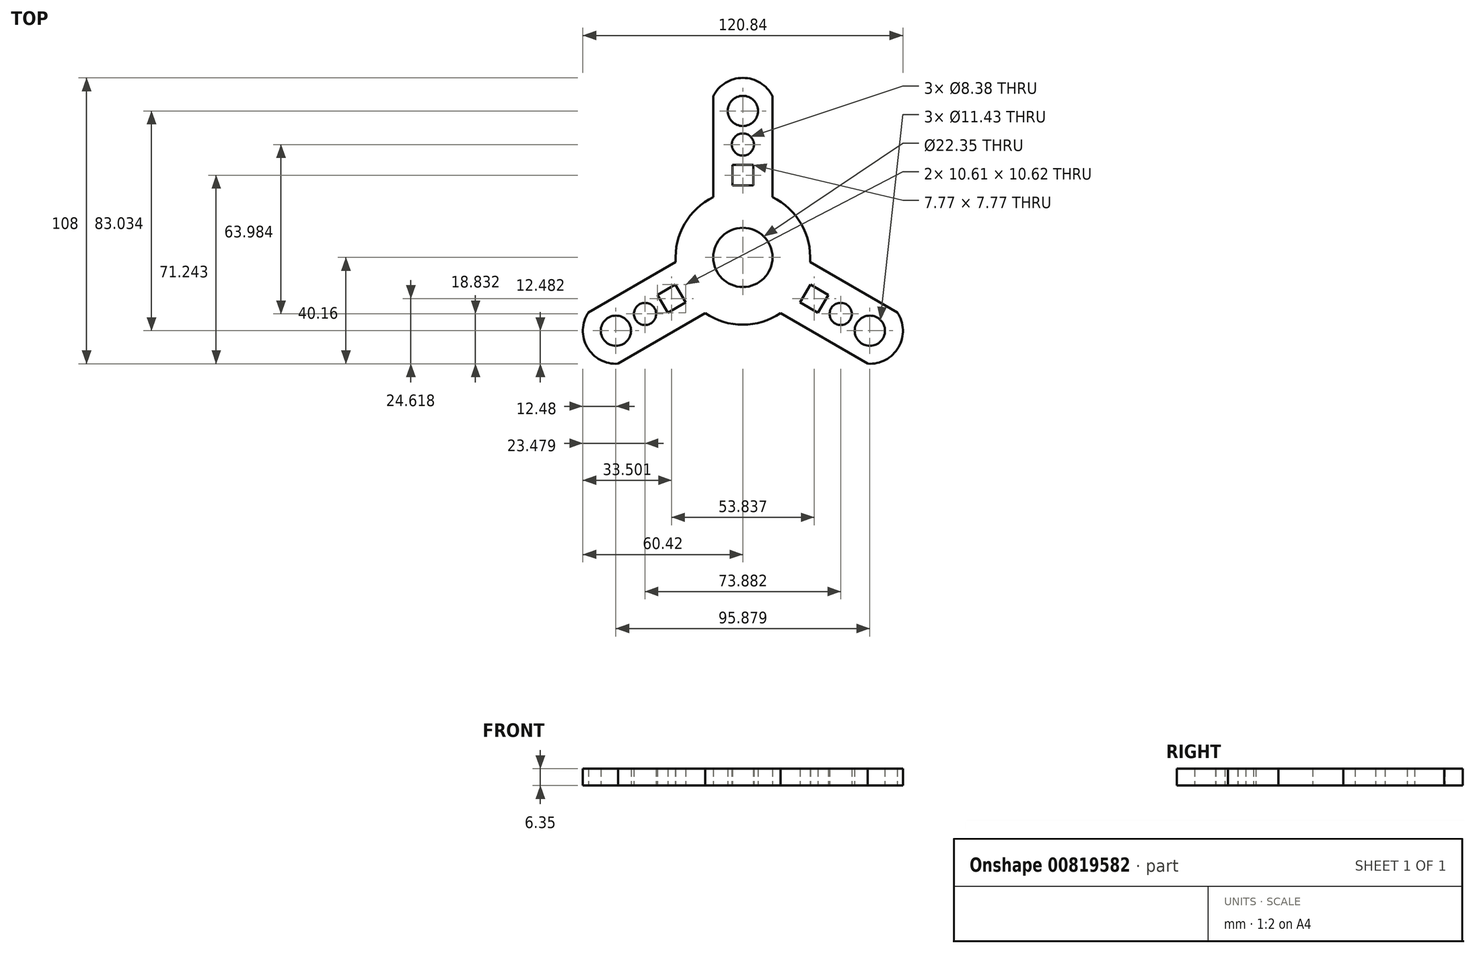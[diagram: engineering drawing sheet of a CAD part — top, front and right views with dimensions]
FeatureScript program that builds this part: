
annotation { "Feature Type Name" : "Feature", "Feature Type Description" : "" }
export const myFeature = defineFeature(function(context is Context, id is Id, definition is map)
    precondition{}
    {
        {
            var Q0;
            Q0=qCreatedBy(makeId("Top.planeOp"),FACE);
            var sketch = newSketch(context, id + "F0", { "sketchPlane" : qUnion([Q0])});
            skCircle(sketch, "E0", {"center": v(0, 0) * mm, "radius": 25.4 * mm});
            skCircle(sketch, "E1", {"center": v(0, 0) * mm, "radius": 11.18 * mm});
            skLineSegment(sketch, "E2", {"start": v(-11.18, 22.8) * mm, "end": v(-11.18, 60.9) * mm});
            skPoint(sketch, "E3.orphan", {"position": v(-11.18, 0) * mm});
            skLineSegment(sketch, "E4.MirrorCS", {"start": v(11.18, 22.8) * mm, "end": v(11.18, 60.9) * mm});
            skArc(sketch, "E5", {"start": v(11.18, 60.9) * mm, "mid": v(0, 67.84) * mm, "end": v(-11.18, 60.9) * mm});
            skCircle(sketch, "E6", {"center": v(0, 55.36) * mm, "radius": 5.72 * mm});
            skCircle(sketch, "E7", {"center": v(0, 42.66) * mm, "radius": 4.2 * mm});
            skLineSegment(sketch, "E8.bottom", {"start": v(-3.89, 34.97) * mm, "end": v(3.89, 34.97) * mm});
            skLineSegment(sketch, "E8.top", {"start": v(-3.89, 27.2) * mm, "end": v(3.89, 27.2) * mm});
            skLineSegment(sketch, "E8.left", {"start": v(-3.89, 34.97) * mm, "end": v(-3.89, 27.2) * mm});
            skLineSegment(sketch, "E8.right", {"start": v(3.89, 34.97) * mm, "end": v(3.89, 27.2) * mm});
            skLineSegment(sketch, "E9.1.0", {"start": v(-25.34, -1.73) * mm, "end": v(-58.34, -20.78) * mm});
            skArc(sketch, "E9.1.1", {"start": v(-58.34, -20.78) * mm, "mid": v(-58.75, -33.92) * mm, "end": v(-47.16, -40.13) * mm});
            skLineSegment(sketch, "E9.1.2", {"start": v(-14.17, -21.08) * mm, "end": v(-47.16, -40.13) * mm});
            skLineSegment(sketch, "E9.1.3", {"start": v(-28.34, -20.85) * mm, "end": v(-32.23, -14.12) * mm});
            skLineSegment(sketch, "E9.1.4", {"start": v(-28.34, -20.85) * mm, "end": v(-21.61, -16.96) * mm});
            skLineSegment(sketch, "E9.1.5", {"start": v(-21.61, -16.96) * mm, "end": v(-25.5, -10.23) * mm});
            skLineSegment(sketch, "E9.1.6", {"start": v(-32.23, -14.12) * mm, "end": v(-25.5, -10.23) * mm});
            skCircle(sketch, "E9.1.7", {"center": v(-36.94, -21.33) * mm, "radius": 4.2 * mm});
            skCircle(sketch, "E9.1.8", {"center": v(-47.94, -27.68) * mm, "radius": 5.72 * mm});
            skLineSegment(sketch, "E9.2.0", {"start": v(14.17, -21.08) * mm, "end": v(47.16, -40.13) * mm});
            skArc(sketch, "E9.2.1", {"start": v(47.16, -40.13) * mm, "mid": v(58.75, -33.92) * mm, "end": v(58.34, -20.78) * mm});
            skLineSegment(sketch, "E9.2.2", {"start": v(25.34, -1.73) * mm, "end": v(58.34, -20.78) * mm});
            skLineSegment(sketch, "E9.2.3", {"start": v(32.23, -14.12) * mm, "end": v(28.34, -20.85) * mm});
            skLineSegment(sketch, "E9.2.4", {"start": v(32.23, -14.12) * mm, "end": v(25.5, -10.23) * mm});
            skLineSegment(sketch, "E9.2.5", {"start": v(25.5, -10.23) * mm, "end": v(21.61, -16.96) * mm});
            skLineSegment(sketch, "E9.2.6", {"start": v(28.34, -20.85) * mm, "end": v(21.61, -16.96) * mm});
            skCircle(sketch, "E9.2.7", {"center": v(36.94, -21.33) * mm, "radius": 4.2 * mm});
            skCircle(sketch, "E9.2.8", {"center": v(47.94, -27.68) * mm, "radius": 5.72 * mm});
            skSolve(sketch);
        }
        {
            var Q0;
            Q0 = qSketchRegion(id + "F0", true);
            extrude(context, id + "F1", {"entities" : qUnion([Q0]), "depth" : 6.35 * mm, "offsetDistance" : 25.4 * mm});
        }
    });
